# Revit family: EBRME-LED-418x-OSRx
name_source: partatom
category: Oprawy oświetleniowe
units: mm (PartAtom-declared; Revit-internal decimal feet)

## family parameters
Numer OmniClass = 23.80.70.11
Obiekt nadrzędny = Powierzchnia
Punkt obliczania pomieszczeń = Nie
Tnij formami wycięć po wczytaniu = Nie
Typ części = Normalny
Tytuł OmniClass = Luminaries for Internal Lighting
Współdzielony = Nie
Wymiar okrągłego złącza = Użyj średnicy
Źródło światła = Tak

## types (8) — shared parameters
Emituj kształt widoczny w renderingu = Nie
Emituj z długości prostokąta = 532 mm  [stored 1.74541 ft]
Emituj z szerokości prostokąta = 534 mm  [stored 1.75197 ft]
Filtr koloru = 16777215
Kod zespołu = D5020200
Lampa = LED
Odchylenie kierunku = 90.00°
Plik sieci fotometrycznej = EBRE-LED 4185200-840 OSR.IES
Producent = RIDI Leuchten GmbH
URL = www.ridi.de
Zmiana temperatury barwowej przyciemniania lampy = <Brak>
brand = RIDI
conformity mark = CE
electrical safety class = 1
height = 90 mm  [stored 0.295276 ft]
ingress protection (IP) code = IP20
length = 597 mm
nominal frequency = 50-60Hz
nominal voltage = 230
voltage type (AC, DC, UC) = AC
weight = 6,2 kg
width = 597 mm
zero-valued in all types: Domyślna rzędna

## per-type parameters (varying)
| type | Model | Obciążenie pozorne | rated input power |
| EBRME-LED 418/2500-830 OSR | 0822874 | 16 VA | 16 |
| EBRME-LED 418/2500-830 OSR-DA | 0832874 | 16 VA | 16 |
| EBRME-LED 418/2700-840 OSR | 0822849 | 16 VA | 16 |
| EBRME-LED 418/2700-840 OSR-DA | 0832849 | 16 VA | 16 |
| EBRME-LED 418/5000-830 OSR | 0822878 | 32 VA | 32 |
| EBRME-LED 418/5000-830 OSR-DA | 0832878 | 32 VA | 32 |
| EBRME-LED 418/5200-840 OSR | 0822830 | 32 VA | 32 |
| EBRME-LED 418/5200-840 OSR-DA | 0832830 | 32 VA | 32 |

note: column(s) folded — value = type name in every type: product name

note: [stored X ft] marks values corroborated as IEEE doubles in the binary element streams (Revit-internal decimal feet)
